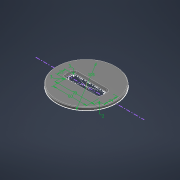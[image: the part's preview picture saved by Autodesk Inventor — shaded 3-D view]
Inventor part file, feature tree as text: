
AUTODESK INVENTOR PART (.ipt)
format: ipt  version: 2022 (Build 260153070, 153G)  size: 153,600 bytes
history: native  units: mm
features: other x3, extrude x2, chamfer x2, sketch x1
ambient origin geometry x8: Origin, YZ Plane, XZ Plane, XY Plane, X Axis, Y Axis, Z Axis, Center Point
bodies: Body1 (feature_tree)
feature tree (8):
  other  "Твердое тело1"
  sketch  "Эскиз1"
  extrude  "Выдавливание1"  Depth=105.0mm
  chamfer  "Фаска1"  Distance=60.0mm
  chamfer  "Фаска2"  Distance=15.0mm
  extrude  "Выдавливание2"  Depth=3.0mm
  other  "РабПлоскость1"
  other  "РабОсь3"
